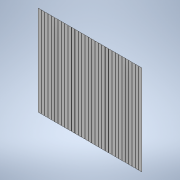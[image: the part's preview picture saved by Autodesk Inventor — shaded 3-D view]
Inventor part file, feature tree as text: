
AUTODESK INVENTOR PART (.ipt)
format: ipt  version: 2021 (Build 250183000, 183)  size: 222,720 bytes
history: native  units: in
note: dims shown in document units (in); Inventor stores cm internally (conversion verified against a paired STEP export)
features: extrude x3, sketch x3, pattern_linear x1, projected_geometry x1
ambient origin geometry x8: Origin, YZ Plane, XZ Plane, XY Plane, X Axis, Y Axis, Z Axis, Center Point
bodies: Solid1 (feature_tree)
feature tree (8):
  extrude  "Extrusion1"  Depth=3.0in
  extrude  "Extrusion2"  Depth=0.1in
  pattern_linear  "Rectangular Pattern1"  Count1=31 Spacing1=0.112in
  extrude  "Extrusion3"  Depth=0.112in TaperAngle=0.0deg
  sketch  "Sketch1"  dims[d0=4.0in d1=3.0in]
  sketch  "Sketch2"  dims[d2=0.04in d3=0.0in d4=0.1in]
  projected_geometry  "Projected Loop1"
  sketch  "Sketch3"  dims[d5=0.0015in d6=0.0in d7=12.2047in d9=0.112in d10=1.0in d11=0.0in]
